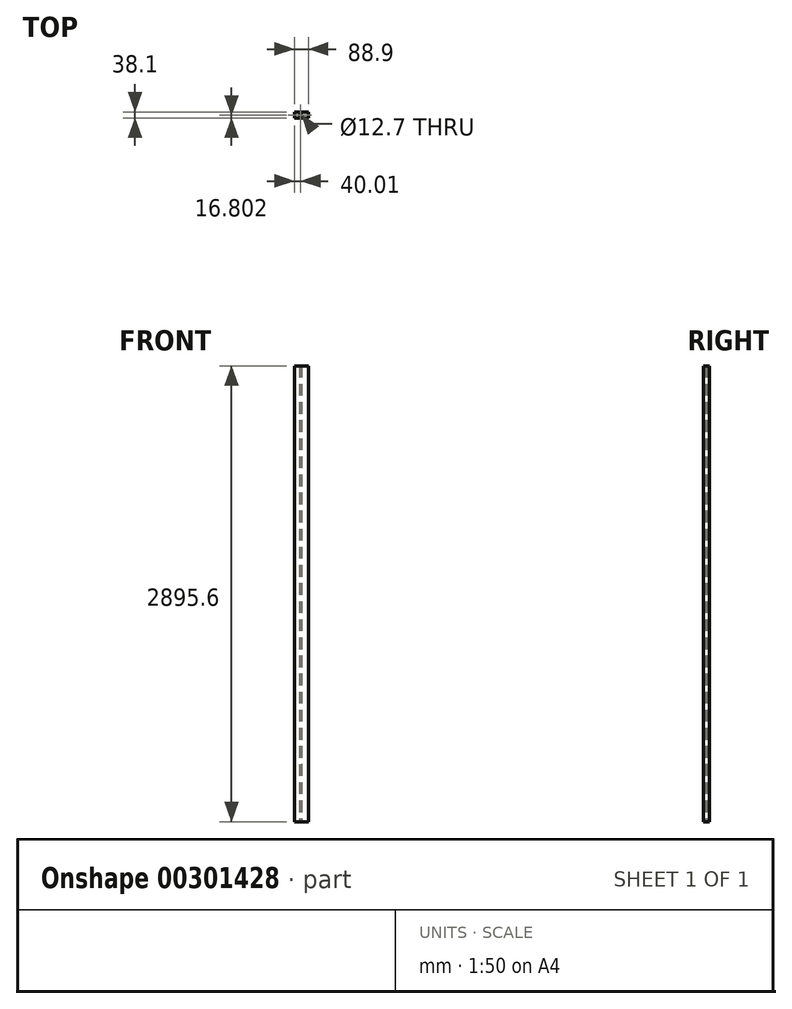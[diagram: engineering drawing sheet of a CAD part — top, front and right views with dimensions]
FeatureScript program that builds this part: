
annotation { "Feature Type Name" : "Feature", "Feature Type Description" : "" }
export const myFeature = defineFeature(function(context is Context, id is Id, definition is map)
    precondition{}
    {
        {
            var Q0;
            Q0=qCreatedBy(makeId("Front.planeOp"),FACE);
            var sketch = newSketch(context, id + "F0", { "sketchPlane" : qUnion([Q0])});
            skLineSegment(sketch, "E0.bottom", {"start": v(-33.39, 2885.24) * mm, "end": v(55.51, 2885.24) * mm});
            skLineSegment(sketch, "E0.top", {"start": v(-33.39, -10.36) * mm, "end": v(55.51, -10.36) * mm});
            skLineSegment(sketch, "E0.left", {"start": v(-33.39, 2885.24) * mm, "end": v(-33.39, -10.36) * mm});
            skLineSegment(sketch, "E0.right", {"start": v(55.51, 2885.24) * mm, "end": v(55.51, -10.36) * mm});
            skSolve(sketch);
        }
        {
            var Q0;
            Q0=makeQuery(id+"F0.imprint","IMPRINT",FACE,{"disambiguationData":[TD([[makeQuery(id+"F0.imprint","IMPRINT",EDGE,{"derivedFrom":sQuery(id+"F0.wireOp",EDGE,"E0.bottom")}),-1.0]])]});
            extrude(context, id + "F1", {"entities" : qUnion([Q0]), "depth" : 38.1 * mm});
        }
        {
            var Q0;
            Q0=makeQuery(id+"F1.opExtrude","SWEPT_FACE",FACE,{"disambiguationData":[OSD([sQuery(id+"F0.wireOp",EDGE,"E0.top")])]});
            var sketch = newSketch(context, id + "F2", { "sketchPlane" : qUnion([Q0])});
            skCircle(sketch, "E1", {"center": v(6.62, 21.3) * mm, "radius": 6.35 * mm});
            skSolve(sketch);
        }
        {
            var Q0;
            Q0=sQuery(id+"F2.wireOp",VERTEX,"E1.center");
            var Q1;
            Q1=makeQuery(id+"F1.opExtrude","SWEPT_BODY",BODY,{"disambiguationData":[OSD([sQuery(id+"F0.wireOp",EDGE,"E0.bottom"),sQuery(id+"F0.wireOp",EDGE,"E0.top"),sQuery(id+"F0.wireOp",EDGE,"E0.left"),sQuery(id+"F0.wireOp",EDGE,"E0.right")])]});
            hole(context, id + "F3", {"style" : HoleStyle.SIMPLE, "endStyle" : HoleEndStyle.THROUGH, "holeDiameter" : 12.7 * mm, "tappedDepth" : 12.7 * mm, "tapClearance" : 3, "locations" : qUnion([Q0]), "scope" : qUnion([Q1])});
        }
    });
